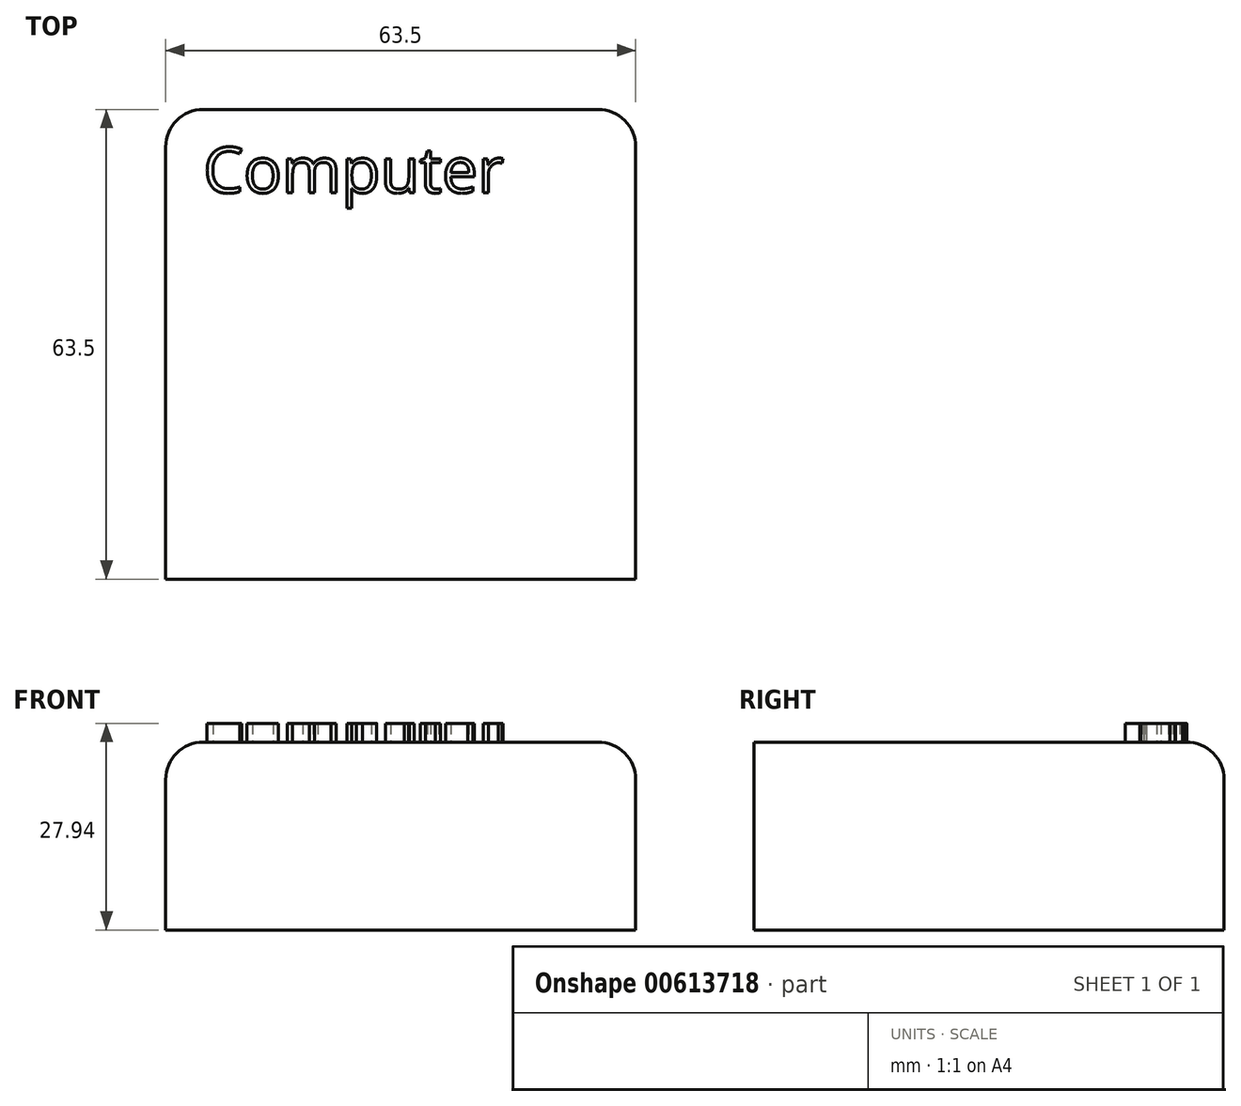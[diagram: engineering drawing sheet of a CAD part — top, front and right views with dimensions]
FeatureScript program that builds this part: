
annotation { "Feature Type Name" : "Feature", "Feature Type Description" : "" }
export const myFeature = defineFeature(function(context is Context, id is Id, definition is map)
    precondition{}
    {
        {
            var Q0;
            Q0=qCreatedBy(makeId("Top.planeOp"),FACE);
            var sketch = newSketch(context, id + "F0", { "sketchPlane" : qUnion([Q0])});
            skLineSegment(sketch, "E0.bottom", {"start": v(-31.75, 31.75) * mm, "end": v(31.75, 31.75) * mm});
            skLineSegment(sketch, "E0.top", {"start": v(-31.75, -31.75) * mm, "end": v(31.75, -31.75) * mm});
            skLineSegment(sketch, "E0.left", {"start": v(-31.75, 31.75) * mm, "end": v(-31.75, -31.75) * mm});
            skLineSegment(sketch, "E0.right", {"start": v(31.75, 31.75) * mm, "end": v(31.75, -31.75) * mm});
            skSolve(sketch);
        }
        {
            var Q0;
            Q0 = qSketchRegion(id + "F0", true);
            extrude(context, id + "F1", {"entities" : qUnion([Q0]), "depth" : 25.4 * mm, "offsetDistance" : 25.4 * mm});
        }
        {
            var Q0;
            Q0=makeQuery(id+"F1.opExtrude","SWEPT_EDGE",EDGE,{"disambiguationData":[OSD([sQuery(id+"F0.wireOp",EDGE,"E0.bottom"),sQuery(id+"F0.wireOp",EDGE,"E0.left")])]});
            var Q1;
            Q1=makeQuery(id+"F1.opExtrude","SWEPT_EDGE",EDGE,{"disambiguationData":[OSD([sQuery(id+"F0.wireOp",EDGE,"E0.bottom"),sQuery(id+"F0.wireOp",EDGE,"E0.right")])]});
            var Q2;
            Q2=makeQuery(id+"F1.opExtrude","CAP_EDGE",EDGE,{"disambiguationData":[OSD([sQuery(id+"F0.wireOp",EDGE,"E0.bottom")])],"isStart":false});
            var Q3;
            Q3=makeQuery(id+"F1.opExtrude","CAP_EDGE",EDGE,{"disambiguationData":[OSD([sQuery(id+"F0.wireOp",EDGE,"E0.left")])],"isStart":false});
            var Q4;
            Q4=makeQuery(id+"F1.opExtrude","CAP_EDGE",EDGE,{"disambiguationData":[OSD([sQuery(id+"F0.wireOp",EDGE,"E0.right")])],"isStart":false});
            fillet(context, id + "F2", {"entities" : qUnion([Q0, Q1, Q2, Q3, Q4]), "radius" : 5.08 * mm, "tangentPropagation" : true, "allowEdgeOverflow" : false});
        }
        {
            var Q0;
            Q0=makeQuery(id+"F1.opExtrude","CAP_FACE",FACE,{"disambiguationData":[OSD([sQuery(id+"F0.wireOp",EDGE,"E0.bottom"),sQuery(id+"F0.wireOp",EDGE,"E0.top"),sQuery(id+"F0.wireOp",EDGE,"E0.left"),sQuery(id+"F0.wireOp",EDGE,"E0.right")])],"isStart":false});
            var sketch = newSketch(context, id + "F3", { "sketchPlane" : qUnion([Q0])});
            skText(sketch, "E1", { "text": "Computer", "fontName": "OpenSans-Regular.ttf"});
            const initialGuessF3  = {"E1": [-0.02667, 0.02047, 1, 0, 0.0062]};
            skSetInitialGuess(sketch, initialGuessF3);
            skSolve(sketch);
        }
        {
            var Q0;
            Q0 = qSketchRegion(id + "F3", true);
            extrude(context, id + "F4", {"entities" : qUnion([Q0]), "operationType" : NewBodyOperationType.ADD, "depth" : 2.54 * mm, "offsetDistance" : 25.4 * mm});
        }
    });
